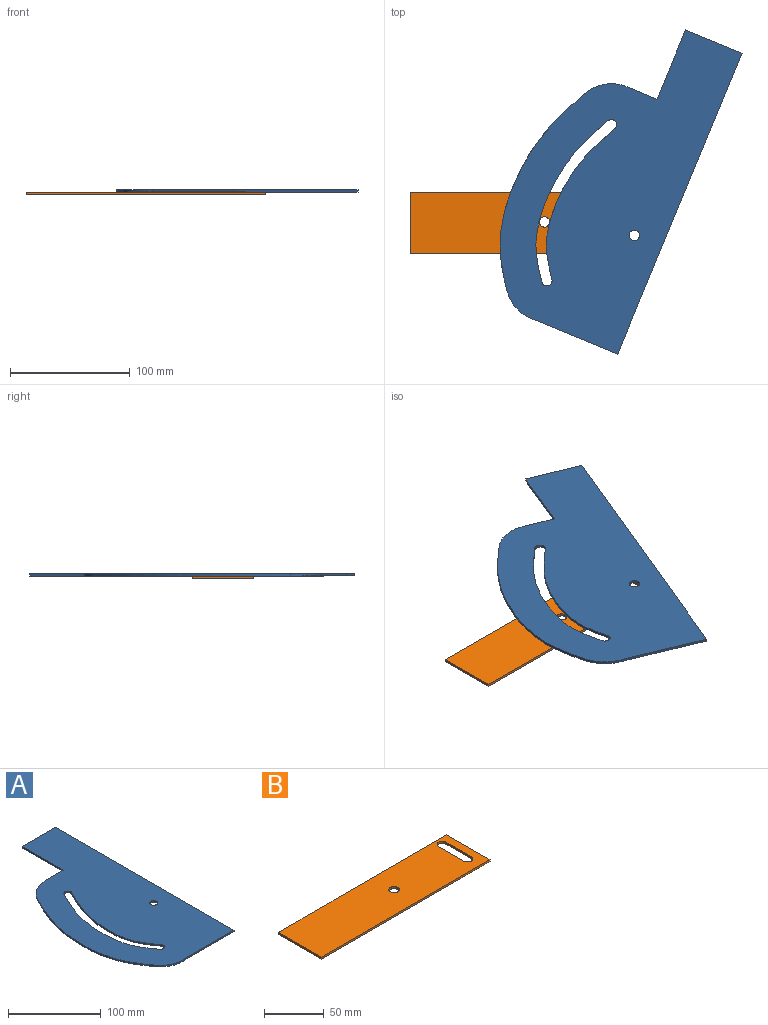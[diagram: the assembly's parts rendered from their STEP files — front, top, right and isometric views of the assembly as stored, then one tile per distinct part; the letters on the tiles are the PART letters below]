
ASSEMBLY  parts=2 mates=1
PART A: 15 faces, bbox 134.4x272.4x2 mm
  f0: extruded ~136.55x21.51mm, area 291.1mm2, adj f1,f12,f13,f14
  f1: cylinder r=4.36mm len=7.86mm, axis (0,0,-1), area 27.4mm2, adj f0,f2,f13,f14
  f2: extruded ~145.6x22.82mm, area 310.2mm2, adj f1,f12,f13,f14
  f3: plane 51x2mm, normal (0,1,0), area 102mm2, adj f4,f11,f13,f14
  f4: plane 62.61x2mm, normal (-1,0,0), area 125.2mm2, adj f3,f5,f13,f14
  f5: plane 27.04x2mm, normal (0,1,0), area 54.1mm2, adj f4,f6,f13,f14
  f6: cylinder r=34.35mm len=30.74mm, axis (0,0,-1), area 76.1mm2, adj f5,f7,f13,f14
  f7: extruded ~176.79x28.67mm, area 376.1mm2, adj f6,f8,f13,f14
  f8: cylinder r=34.35mm len=32.27mm, axis (0,0,-1), area 73.5mm2, adj f7,f9,f13,f14
  f9: plane 73.41x2mm, normal (0,-1,0), area 146.8mm2, adj f8,f11,f13,f14
  f10: cylinder r=4.36mm len=8.71mm, axis (0,0,-1), area 54.7mm2, adj f13,f14
  f11: plane 272.09x2mm, normal (1,0,0), area 544.2mm2, adj f3,f9,f13,f14
  f12: cylinder r=4.36mm len=8.25mm, axis (0,0,-1), area 27.4mm2, adj f0,f2,f13,f14
  f13: plane 272.4x134.36mm, normal (0,0,1), area 27245mm2, adj f0,f1,f2,f3,f4,f5,f6,f7
  f14: plane 272.4x134.36mm, normal (0,0,-1), area 27245mm2, adj f0,f1,f2,f3,f4,f5,f6,f7
PART B: 11 faces, bbox 200x51x2 mm
  f0: plane 51x2mm, normal (1,0,0), area 102mm2, adj f1,f8,f9,f10
  f1: plane 200x2mm, normal (0,1,0), area 400mm2, adj f0,f2,f9,f10
  f2: plane 51x2mm, normal (-1,0,0), area 102mm2, adj f1,f8,f9,f10
  f3: plane 30x2mm, normal (1,0,0), area 60mm2, adj f4,f6,f9,f10
  f4: cylinder r=4.36mm len=8.71mm, axis (0,0,1), area 27.4mm2, adj f3,f5,f9,f10
  f5: plane 30x2mm, normal (-1,0,0), area 60mm2, adj f4,f6,f9,f10
  f6: cylinder r=4.36mm len=8.71mm, axis (0,0,1), area 27.4mm2, adj f3,f5,f9,f10
  f7: cylinder r=4.36mm len=8.71mm, axis (0,0,1), area 54.7mm2, adj f9,f10
  f8: plane 200x2mm, normal (0,-1,0), area 400mm2, adj f0,f2,f9,f10
  f9: plane 200x51mm, normal (0,0,-1), area 9819.5mm2, adj f0,f1,f2,f3,f4,f5,f6,f7
  f10: plane 200x51mm, normal (0,0,1), area 9819.5mm2, adj f0,f1,f2,f3,f4,f5,f6,f7
PLACE A rot(axis=(0,0,-1),22.5deg) t=(7.66,-22.59,0)mm
PLACE B at identity fixed
MATE pin_slot A.f10 <-> B.f6  axis (0,0,-1) through (-25,-36.14,0)mm
